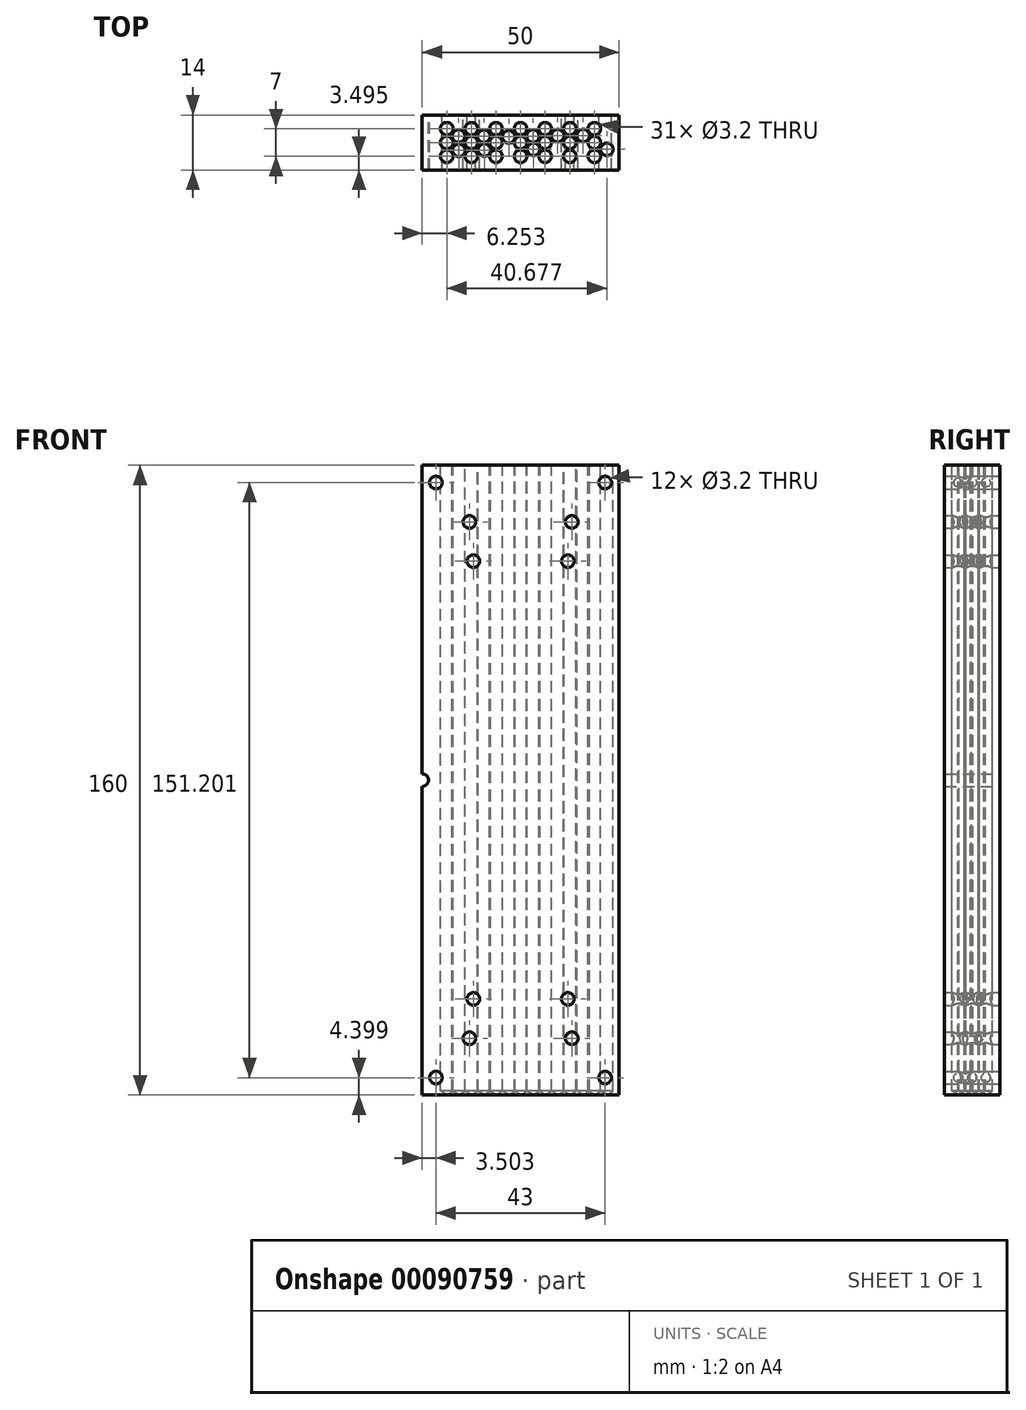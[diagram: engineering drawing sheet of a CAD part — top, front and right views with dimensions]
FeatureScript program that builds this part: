
annotation { "Feature Type Name" : "Feature", "Feature Type Description" : "" }
export const myFeature = defineFeature(function(context is Context, id is Id, definition is map)
    precondition{}
    {
        {
            var Q0;
            Q0=qCreatedBy(makeId("Top.planeOp"),FACE);
            var sketch = newSketch(context, id + "F0", { "sketchPlane" : qUnion([Q0])});
            skLineSegment(sketch, "E0.bottom", {"start": v(11.2, 34.59) * mm, "end": v(61.2, 34.59) * mm});
            skLineSegment(sketch, "E0.top", {"start": v(11.2, 20.59) * mm, "end": v(61.2, 20.59) * mm});
            skLineSegment(sketch, "E0.left", {"start": v(11.2, 34.59) * mm, "end": v(11.2, 20.59) * mm});
            skLineSegment(sketch, "E0.right", {"start": v(61.2, 34.59) * mm, "end": v(61.2, 20.59) * mm});
            skSolve(sketch);
        }
        {
            var Q0;
            Q0=makeQuery(id+"F0.imprint","IMPRINT",FACE,{"disambiguationData":[TD([[makeQuery(id+"F0.imprint","IMPRINT",EDGE,{"derivedFrom":sQuery(id+"F0.wireOp",EDGE,"E0.bottom")}),-1.0]])]});
            extrude(context, id + "F1", {"entities" : qUnion([Q0]), "depth" : 160 * mm});
        }
        {
            var Q0;
            Q0=makeQuery(id+"F1.opExtrude","CAP_FACE",FACE,{"disambiguationData":[OSD([sQuery(id+"F0.wireOp",EDGE,"E0.bottom"),sQuery(id+"F0.wireOp",EDGE,"E0.top"),sQuery(id+"F0.wireOp",EDGE,"E0.left"),sQuery(id+"F0.wireOp",EDGE,"E0.right")])],"isStart":false});
            var sketch = newSketch(context, id + "F2", { "sketchPlane" : qUnion([Q0])});
            skPoint(sketch, "E1.startSnap0", {"position": v(11.2, 27.59) * mm});
            skPoint(sketch, "E1.startSnap1", {"position": v(36.2, 34.59) * mm});
            skPoint(sketch, "E2", {"position": v(48.7, 27.59) * mm});
            skPoint(sketch, "E3.orphan", {"position": v(36.2, 27.59) * mm});
            skPoint(sketch, "E1.end.orphan", {"position": v(61.2, 27.59) * mm});
            skLineSegment(sketch, "E4", {"start": v(48.7, 27.59) * mm, "end": v(36.2, 27.59) * mm, "construction": true});
            skPoint(sketch, "E5", {"position": v(42.44, 27.59) * mm});
            skLineSegment(sketch, "E6", {"start": v(48.7, 27.59) * mm, "end": v(61.2, 27.59) * mm, "construction": true});
            skPoint(sketch, "E7", {"position": v(54.94, 27.59) * mm});
            skLineSegment(sketch, "E8", {"start": v(36.2, 34.59) * mm, "end": v(36.2, 20.59) * mm, "construction": true});
            skPoint(sketch, "E9.MirrorP", {"position": v(17.44, 27.59) * mm});
            skPoint(sketch, "E10.MirrorP", {"position": v(23.7, 27.59) * mm});
            skPoint(sketch, "E11.MirrorP", {"position": v(29.94, 27.59) * mm});
            skLineSegment(sketch, "E12", {"start": v(61.2, 27.59) * mm, "end": v(61.2, 20.59) * mm, "construction": true});
            skLineSegment(sketch, "E13", {"start": v(61.2, 24.09) * mm, "end": v(61.2, 27.59) * mm});
            skLineSegment(sketch, "E14", {"start": v(61.2, 25.84) * mm, "end": v(36.2, 25.84) * mm});
            skPoint(sketch, "E15.MirrorP", {"position": v(17.44, 24.09) * mm});
            skPoint(sketch, "E16.MirrorP", {"position": v(23.7, 24.09) * mm});
            skPoint(sketch, "E17.MirrorP", {"position": v(29.94, 24.09) * mm});
            skPoint(sketch, "E18.MirrorP", {"position": v(36.2, 24.09) * mm});
            skPoint(sketch, "E19.MirrorP", {"position": v(42.44, 24.09) * mm});
            skPoint(sketch, "E20.MirrorP", {"position": v(48.7, 24.09) * mm});
            skPoint(sketch, "E21.MirrorP", {"position": v(54.94, 24.09) * mm});
            skPoint(sketch, "E22.MirrorP", {"position": v(17.44, 31.09) * mm});
            skPoint(sketch, "E23.MirrorP", {"position": v(23.7, 31.09) * mm});
            skPoint(sketch, "E24.MirrorP", {"position": v(29.94, 31.09) * mm});
            skPoint(sketch, "E25.MirrorP", {"position": v(36.2, 31.09) * mm});
            skPoint(sketch, "E26.MirrorP", {"position": v(42.44, 31.09) * mm});
            skPoint(sketch, "E27.MirrorP", {"position": v(48.7, 31.09) * mm});
            skPoint(sketch, "E28.MirrorP", {"position": v(54.94, 31.09) * mm});
            skPoint(sketch, "E29", {"position": v(52.3, 25.84) * mm});
            skPoint(sketch, "E30", {"position": v(52.1, 29.34) * mm});
            skPoint(sketch, "E31", {"position": v(45.62, 29.32) * mm});
            skPoint(sketch, "E32", {"position": v(39.34, 29.23) * mm});
            skPoint(sketch, "E33", {"position": v(33.19, 29) * mm});
            skPoint(sketch, "E34", {"position": v(26.84, 29.18) * mm});
            skPoint(sketch, "E35", {"position": v(20.44, 29.22) * mm});
            skPoint(sketch, "E36", {"position": v(20.5, 25.6) * mm});
            skPoint(sketch, "E37", {"position": v(26.98, 25.7) * mm});
            skPoint(sketch, "E38", {"position": v(33, 25.65) * mm});
            skPoint(sketch, "E39", {"position": v(39.47, 25.84) * mm});
            skPoint(sketch, "E40", {"position": v(58.12, 25.84) * mm});
            skSolve(sketch);
        }
        {
            var Q0;
            Q0=sQuery(id+"F2.wireOp",VERTEX,"E23.MirrorP");
            var Q1;
            Q1=sQuery(id+"F2.wireOp",VERTEX,"E39");
            var Q2;
            Q2=sQuery(id+"F2.wireOp",VERTEX,"E11.MirrorP");
            var Q3;
            Q3=sQuery(id+"F2.wireOp",VERTEX,"E25.MirrorP");
            var Q4;
            Q4=sQuery(id+"F2.wireOp",VERTEX,"E30");
            var Q5;
            Q5=sQuery(id+"F2.wireOp",VERTEX,"E37");
            var Q6;
            Q6=sQuery(id+"F2.wireOp",VERTEX,"E21.MirrorP");
            var Q7;
            Q7=sQuery(id+"F2.wireOp",VERTEX,"E31");
            var Q8;
            Q8=sQuery(id+"F2.wireOp",VERTEX,"E3.orphan");
            var Q9;
            Q9=sQuery(id+"F2.wireOp",VERTEX,"E15.MirrorP");
            var Q10;
            Q10=sQuery(id+"F2.wireOp",VERTEX,"E28.MirrorP");
            var Q11;
            Q11=sQuery(id+"F2.wireOp",VERTEX,"E10.MirrorP");
            var Q12;
            Q12=sQuery(id+"F2.wireOp",VERTEX,"E27.MirrorP");
            var Q13;
            Q13=sQuery(id+"F2.wireOp",VERTEX,"E9.MirrorP");
            var Q14;
            Q14=sQuery(id+"F2.wireOp",VERTEX,"E40");
            var Q15;
            Q15=sQuery(id+"F2.wireOp",VERTEX,"E22.MirrorP");
            var Q16;
            Q16=sQuery(id+"F2.wireOp",VERTEX,"E18.MirrorP");
            var Q17;
            Q17=sQuery(id+"F2.wireOp",VERTEX,"E34");
            var Q18;
            Q18=sQuery(id+"F2.wireOp",VERTEX,"E35");
            var Q19;
            Q19=sQuery(id+"F2.wireOp",VERTEX,"E17.MirrorP");
            var Q20;
            Q20=sQuery(id+"F2.wireOp",VERTEX,"E19.MirrorP");
            var Q21;
            Q21=sQuery(id+"F2.wireOp",VERTEX,"E33");
            var Q22;
            Q22=sQuery(id+"F2.wireOp",VERTEX,"E36");
            var Q23;
            Q23=sQuery(id+"F2.wireOp",VERTEX,"E16.MirrorP");
            var Q24;
            Q24=sQuery(id+"F2.wireOp",VERTEX,"E20.MirrorP");
            var Q25;
            Q25=sQuery(id+"F2.wireOp",VERTEX,"E32");
            var Q26;
            Q26=sQuery(id+"F2.wireOp",VERTEX,"E2");
            var Q27;
            Q27=sQuery(id+"F2.wireOp",VERTEX,"E7");
            var Q28;
            Q28=sQuery(id+"F2.wireOp",VERTEX,"E5");
            var Q29;
            Q29=sQuery(id+"F2.wireOp",VERTEX,"E24.MirrorP");
            var Q30;
            Q30=sQuery(id+"F2.wireOp",VERTEX,"E26.MirrorP");
            var Q31;
            Q31=makeQuery(id+"F1.opExtrude","SWEPT_BODY",BODY,{"disambiguationData":[OSD([sQuery(id+"F0.wireOp",EDGE,"E0.bottom"),sQuery(id+"F0.wireOp",EDGE,"E0.top"),sQuery(id+"F0.wireOp",EDGE,"E0.left"),sQuery(id+"F0.wireOp",EDGE,"E0.right")])]});
            hole(context, id + "F3", {"style" : HoleStyle.SIMPLE, "endStyle" : HoleEndStyle.BLIND, "holeDiameter" : 3.2 * mm, "holeDepth" : 159 * mm, "locations" : qUnion([Q0, Q1, Q2, Q3, Q4, Q5, Q6, Q7, Q8, Q9, Q10, Q11, Q12, Q13, Q14, Q15, Q16, Q17, Q18, Q19, Q20, Q21, Q22, Q23, Q24, Q25, Q26, Q27, Q28, Q29, Q30]), "scope" : qUnion([Q31])});
        }
        {
            var Q0;
            Q0=makeQuery(id+"F1.opExtrude","SWEPT_FACE",FACE,{"disambiguationData":[OSD([sQuery(id+"F0.wireOp",EDGE,"E0.bottom")])]});
            var sketch = newSketch(context, id + "F4", { "sketchPlane" : qUnion([Q0])});
            skPoint(sketch, "E41", {"position": v(-14.7, 4.4) * mm});
            skLineSegment(sketch, "E42", {"start": v(-36.2, 0) * mm, "end": v(-36.2, 225.29) * mm, "construction": true});
            skPoint(sketch, "E42.endSnap0", {"position": v(-36.2, 160) * mm});
            skLineSegment(sketch, "E43", {"start": v(-11.2, 80) * mm, "end": v(-117.06, 80) * mm, "construction": true});
            skPoint(sketch, "E43.endSnap0", {"position": v(-61.2, 80) * mm});
            skPoint(sketch, "E44.MirrorP", {"position": v(-57.7, 4.4) * mm});
            skPoint(sketch, "E45.MirrorP", {"position": v(-57.7, 155.6) * mm});
            skPoint(sketch, "E46.MirrorP", {"position": v(-14.7, 155.6) * mm});
            skPoint(sketch, "E47", {"position": v(-24.2, 24.4) * mm});
            skPoint(sketch, "E48", {"position": v(-23.2, 14.4) * mm});
            skPoint(sketch, "E49.MirrorP", {"position": v(-48.2, 24.4) * mm});
            skPoint(sketch, "E50.MirrorP", {"position": v(-49.2, 14.4) * mm});
            skPoint(sketch, "E51.MirrorP", {"position": v(-24.2, 135.6) * mm});
            skPoint(sketch, "E52.MirrorP", {"position": v(-49.2, 145.6) * mm});
            skPoint(sketch, "E53.MirrorP", {"position": v(-48.2, 135.6) * mm});
            skPoint(sketch, "E54.MirrorP", {"position": v(-23.2, 145.6) * mm});
            skSolve(sketch);
        }
        {
            var Q0;
            Q0=sQuery(id+"F4.wireOp",VERTEX,"E51.MirrorP");
            var Q1;
            Q1=sQuery(id+"F4.wireOp",VERTEX,"E49.MirrorP");
            var Q2;
            Q2=sQuery(id+"F4.wireOp",VERTEX,"E53.MirrorP");
            var Q3;
            Q3=sQuery(id+"F4.wireOp",VERTEX,"E52.MirrorP");
            var Q4;
            Q4=sQuery(id+"F4.wireOp",VERTEX,"E48");
            var Q5;
            Q5=sQuery(id+"F4.wireOp",VERTEX,"E46.MirrorP");
            var Q6;
            Q6=sQuery(id+"F4.wireOp",VERTEX,"E54.MirrorP");
            var Q7;
            Q7=sQuery(id+"F4.wireOp",VERTEX,"E50.MirrorP");
            var Q8;
            Q8=sQuery(id+"F4.wireOp",VERTEX,"E47");
            var Q9;
            Q9=sQuery(id+"F4.wireOp",VERTEX,"E41");
            var Q10;
            Q10=sQuery(id+"F4.wireOp",VERTEX,"E45.MirrorP");
            var Q11;
            Q11=sQuery(id+"F4.wireOp",VERTEX,"E44.MirrorP");
            var Q12;
            Q12=sQuery(id+"F4.wireOp",VERTEX,"E43.start");
            var Q13;
            Q13=makeQuery(id+"F1.opExtrude","SWEPT_BODY",BODY,{"disambiguationData":[OSD([sQuery(id+"F0.wireOp",EDGE,"E0.bottom"),sQuery(id+"F0.wireOp",EDGE,"E0.top"),sQuery(id+"F0.wireOp",EDGE,"E0.left"),sQuery(id+"F0.wireOp",EDGE,"E0.right")])]});
            hole(context, id + "F5", {"style" : HoleStyle.SIMPLE, "endStyle" : HoleEndStyle.BLIND, "holeDiameter" : 3.2 * mm, "holeDepth" : 160 * mm, "locations" : qUnion([Q0, Q1, Q2, Q3, Q4, Q5, Q6, Q7, Q8, Q9, Q10, Q11, Q12]), "scope" : qUnion([Q13])});
        }
    });
